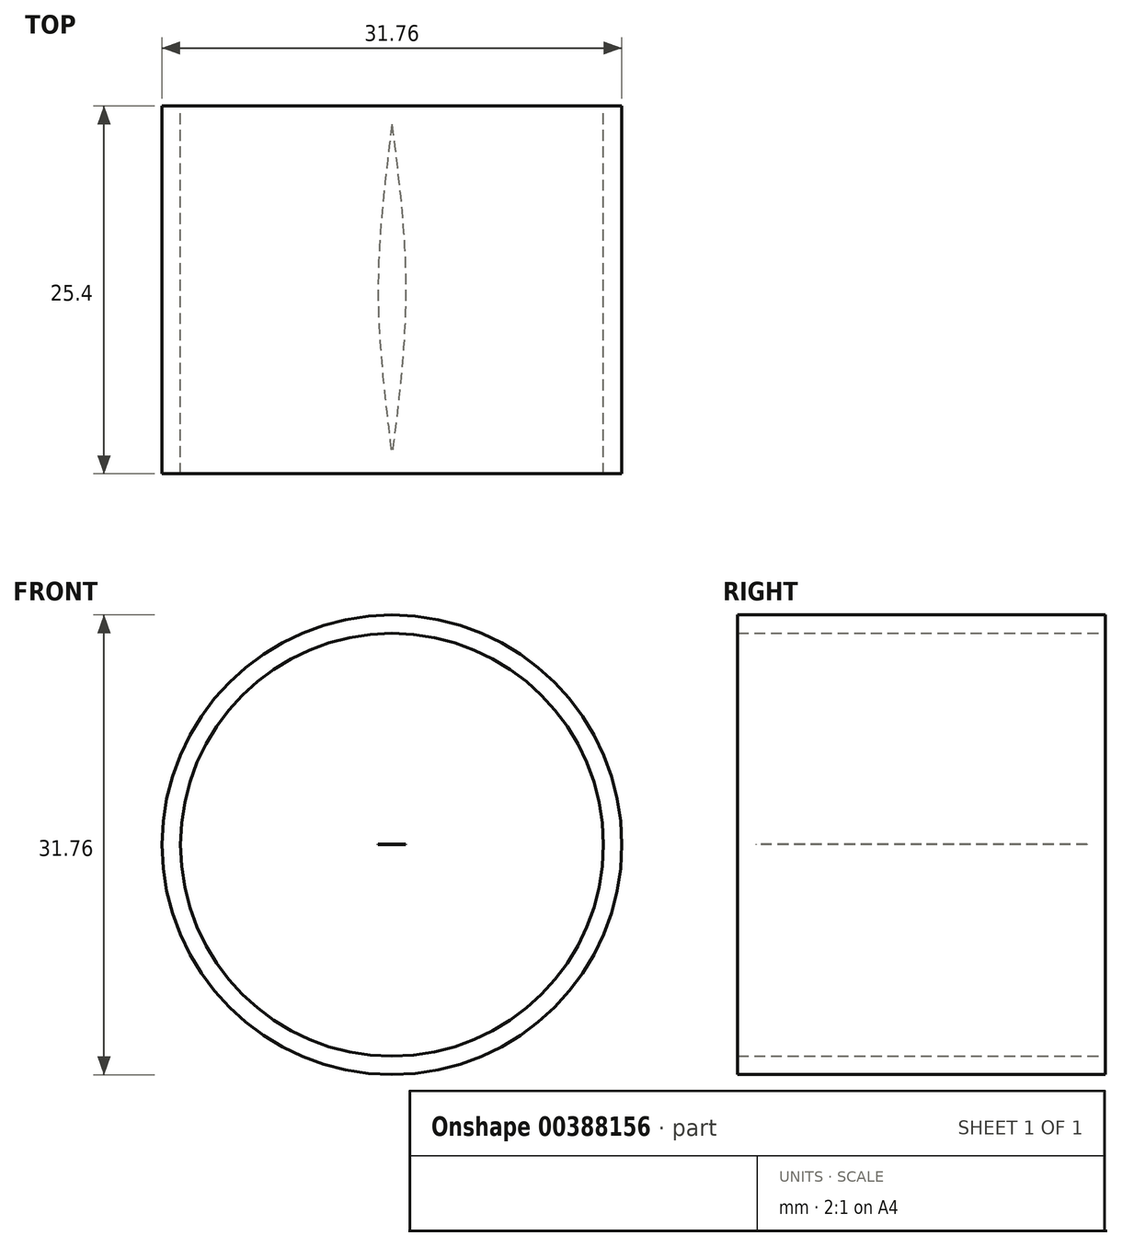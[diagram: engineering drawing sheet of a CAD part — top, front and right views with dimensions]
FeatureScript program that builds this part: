
annotation { "Feature Type Name" : "Feature", "Feature Type Description" : "" }
export const myFeature = defineFeature(function(context is Context, id is Id, definition is map)
    precondition{}
    {
        {
            var Q0;
            Q0=qCreatedBy(makeId("Front.planeOp"),FACE);
            var sketch = newSketch(context, id + "F0", { "sketchPlane" : qUnion([Q0])});
            skCircle(sketch, "E0", {"center": v(0, 0) * mm, "radius": 14.6 * mm});
            skCircle(sketch, "E1", {"center": v(0, 0) * mm, "radius": 15.88 * mm});
            skSolve(sketch);
        }
        {
            var Q0;
            Q0 = qSketchRegion(id + "F0", true);
            extrude(context, id + "F1", {"entities" : qUnion([Q0]), "depth" : 25.4 * mm});
        }
        {
            var Q0;
            Q0=qCreatedBy(makeId("Top.planeOp"),FACE);
            cPlane(context, id + "F2", {"entities" : qUnion([Q0]), "cplaneType" : CPlaneType.OFFSET, "offset" : 1.25 / 50.8 * mm, "width" : 152.4 * mm, "height" : 152.4 * mm});
        }
        {
            var Q0;
            Q0=qCreatedBy(id+"F2.planeOp",FACE);
            var sketch = newSketch(context, id + "F3", { "sketchPlane" : qUnion([Q0])});
            skLineSegment(sketch, "E2", {"start": v(15.88, 0) * mm, "end": v(15.88, -25.4) * mm});
            skLineSegment(sketch, "E3", {"start": v(-15.88, -25.4) * mm, "end": v(-15.88, 0) * mm});
            skLineSegment(sketch, "E4", {"start": v(-15.88, -12.7) * mm, "end": v(15.88, -12.7) * mm});
            skLineSegment(sketch, "E5.bottom", {"start": v(0.95, -1.27) * mm, "end": v(-0.95, -1.27) * mm});
            skLineSegment(sketch, "E5.top", {"start": v(0.95, -24.13) * mm, "end": v(-0.95, -24.13) * mm});
            skLineSegment(sketch, "E5.left", {"start": v(0.95, -1.27) * mm, "end": v(0.95, -24.13) * mm});
            skLineSegment(sketch, "E5.right", {"start": v(-0.95, -1.27) * mm, "end": v(-0.95, -24.13) * mm});
            skPoint(sketch, "E5.middle", {"position": v(0, -12.7) * mm});
            skFitSpline(sketch, "E6", {"points": [v(0, -1.27) * mm, v(0.95, -12.7) * mm, v(0, -24.13) * mm], "startDerivative": vector(2.86, -22.86) * mm, "endDerivative": vector(-2.86, -22.86) * mm});
            skFitSpline(sketch, "E7.MirrorCS", {"points": [v(0, -1.27) * mm, v(-0.95, -12.7) * mm, v(0, -24.13) * mm], "startDerivative": vector(-2.86, -22.86) * mm, "endDerivative": vector(2.86, -22.86) * mm});
            skSolve(sketch);
        }
        {
            var Q0;
            {var subQ0=sQuery(id+"F3.wireOp",EDGE,"E6");var subQ1=sQuery(id+"F3.wireOp",EDGE,"E4");var subQ2=makeQuery(id+"F3.imprint","INTERSECT",VERTEX,{"derivedFrom":[subQ1,sQuery(id+"F3.wireOp",EDGE,"E5.left"),subQ0]});Q0=makeQuery(id+"F3.imprint","IMPRINT",FACE,{"disambiguationData":[TD([[makeQuery(id+"F3.imprint","IMPRINT",EDGE,{"disambiguationData":[TD([[subQ2,1.0]])],"derivedFrom":subQ1}),1.0]])]});}
            var Q1;
            {var subQ0=sQuery(id+"F3.wireOp",EDGE,"E6");var subQ1=sQuery(id+"F3.wireOp",EDGE,"E4");var subQ2=makeQuery(id+"F3.imprint","INTERSECT",VERTEX,{"derivedFrom":[subQ1,sQuery(id+"F3.wireOp",EDGE,"E5.left"),subQ0]});Q1=makeQuery(id+"F3.imprint","IMPRINT",FACE,{"disambiguationData":[TD([[makeQuery(id+"F3.imprint","IMPRINT",EDGE,{"disambiguationData":[TD([[subQ2,1.0]])],"derivedFrom":subQ1}),-1.0]])]});}
            extrude(context, id + "F4", {"entities" : qUnion([Q0, Q1]), "operationType" : NewBodyOperationType.ADD, "depth" : (3 - 1.25) / 50.8 * mm});
        }
    });
